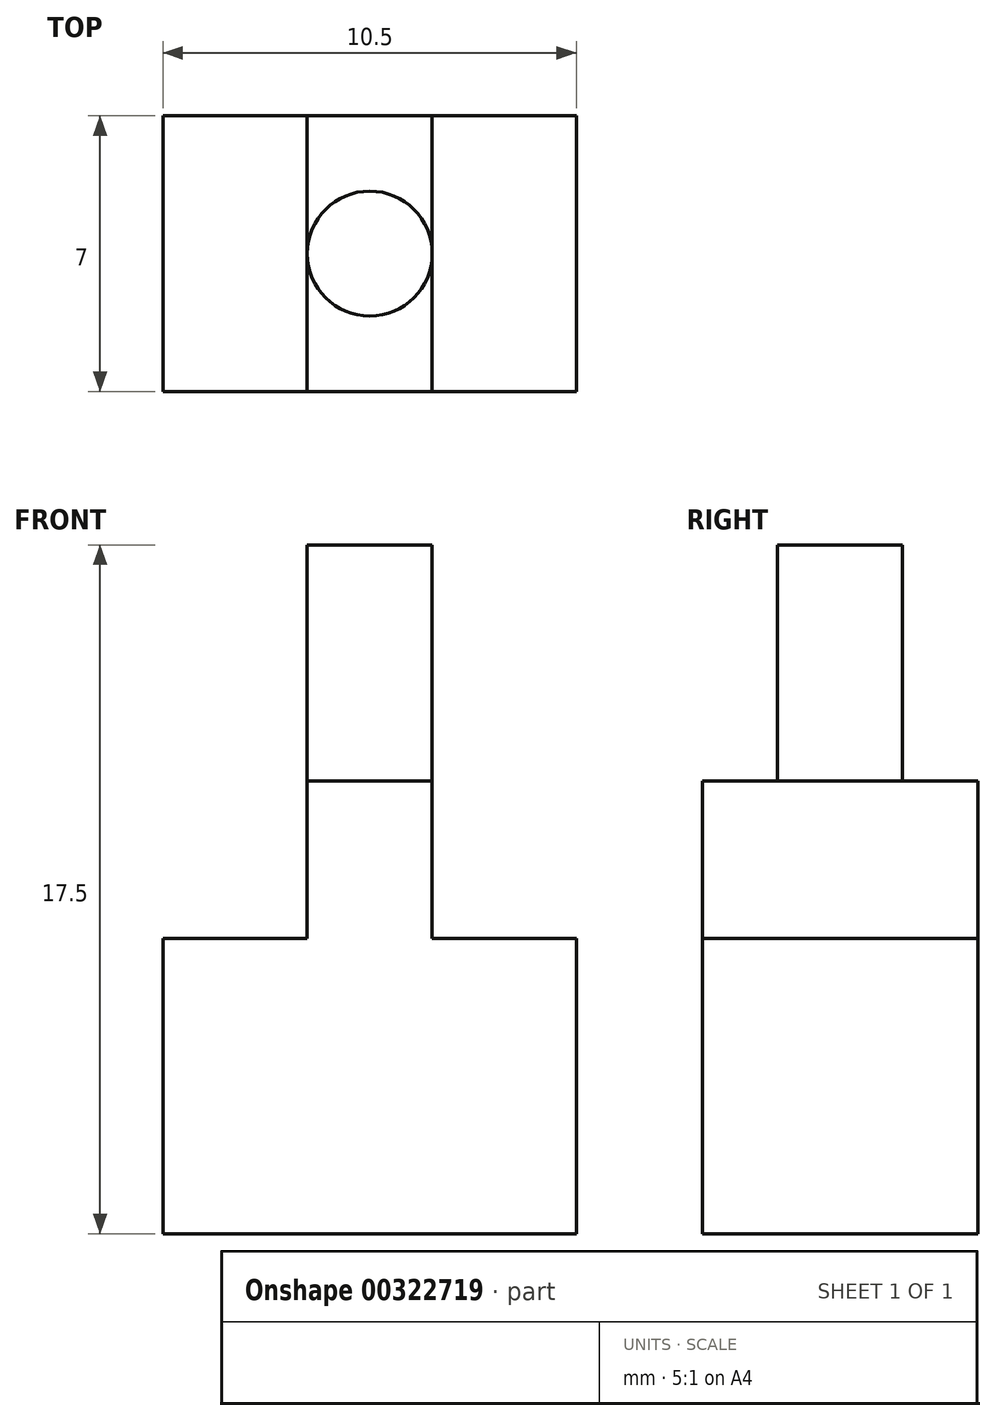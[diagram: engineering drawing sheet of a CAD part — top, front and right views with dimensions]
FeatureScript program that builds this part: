
annotation { "Feature Type Name" : "Feature", "Feature Type Description" : "" }
export const myFeature = defineFeature(function(context is Context, id is Id, definition is map)
    precondition{}
    {
        {
            assignVariable(context, id + "F0", {"name" : "wood", "anyValue" : 6});
        }
        {
            var Q0;
            Q0=qCreatedBy(makeId("Front.planeOp"),FACE);
            var sketch = newSketch(context, id + "F1", { "sketchPlane" : qUnion([Q0])});
            skLineSegment(sketch, "E0", {"start": v(1.59, 0) * mm, "end": v(1.59, -4) * mm});
            skLineSegment(sketch, "E1", {"start": v(1.59, -4) * mm, "end": v(5.25, -4) * mm});
            skLineSegment(sketch, "E2", {"start": v(5.25, -4) * mm, "end": v(5.25, -11.5) * mm});
            skLineSegment(sketch, "E3.MirrorCS", {"start": v(-5.25, -4) * mm, "end": v(-5.25, -11.5) * mm});
            skLineSegment(sketch, "E4.MirrorCS", {"start": v(-1.59, -4) * mm, "end": v(-5.25, -4) * mm});
            skLineSegment(sketch, "E5.MirrorCS", {"start": v(-1.59, 0) * mm, "end": v(-1.59, -4) * mm});
            skLineSegment(sketch, "E6", {"start": v(5.25, -11.5) * mm, "end": v(-5.25, -11.5) * mm});
            skLineSegment(sketch, "E7", {"start": v(-1.59, 0) * mm, "end": v(1.59, 0) * mm});
            skSolve(sketch);
        }
        {
            var Q0;
            Q0=makeQuery(id+"F1.imprint","IMPRINT",FACE,{"disambiguationData":[TD([[makeQuery(id+"F1.imprint","IMPRINT",EDGE,{"derivedFrom":sQuery(id+"F1.wireOp",EDGE,"E0")}),-1.0]])]});
            extrude(context, id + "F2", {"entities" : qUnion([Q0]), "depth" : (getVariable(context, 'wood') + 1) * mm, "offsetDistance" : 25 * mm, "symmetric" : true});
        }
        {
            var Q0;
            Q0=qCreatedBy(makeId("Top.planeOp"),FACE);
            var sketch = newSketch(context, id + "F3", { "sketchPlane" : qUnion([Q0])});
            skCircle(sketch, "E8", {"center": v(0, 0) * mm, "radius": 1.59 * mm});
            skSolve(sketch);
        }
        {
            var Q0;
            Q0=makeQuery(id+"F3.imprint","IMPRINT",FACE,{"disambiguationData":[TD([[makeQuery(id+"F3.imprint","IMPRINT",EDGE,{"derivedFrom":sQuery(id+"F3.wireOp",EDGE,"E8")}),1.0]])]});
            extrude(context, id + "F4", {"entities" : qUnion([Q0]), "operationType" : NewBodyOperationType.ADD, "depth" : (getVariable(context, 'wood')) * mm, "offsetDistance" : 25 * mm});
        }
    });
